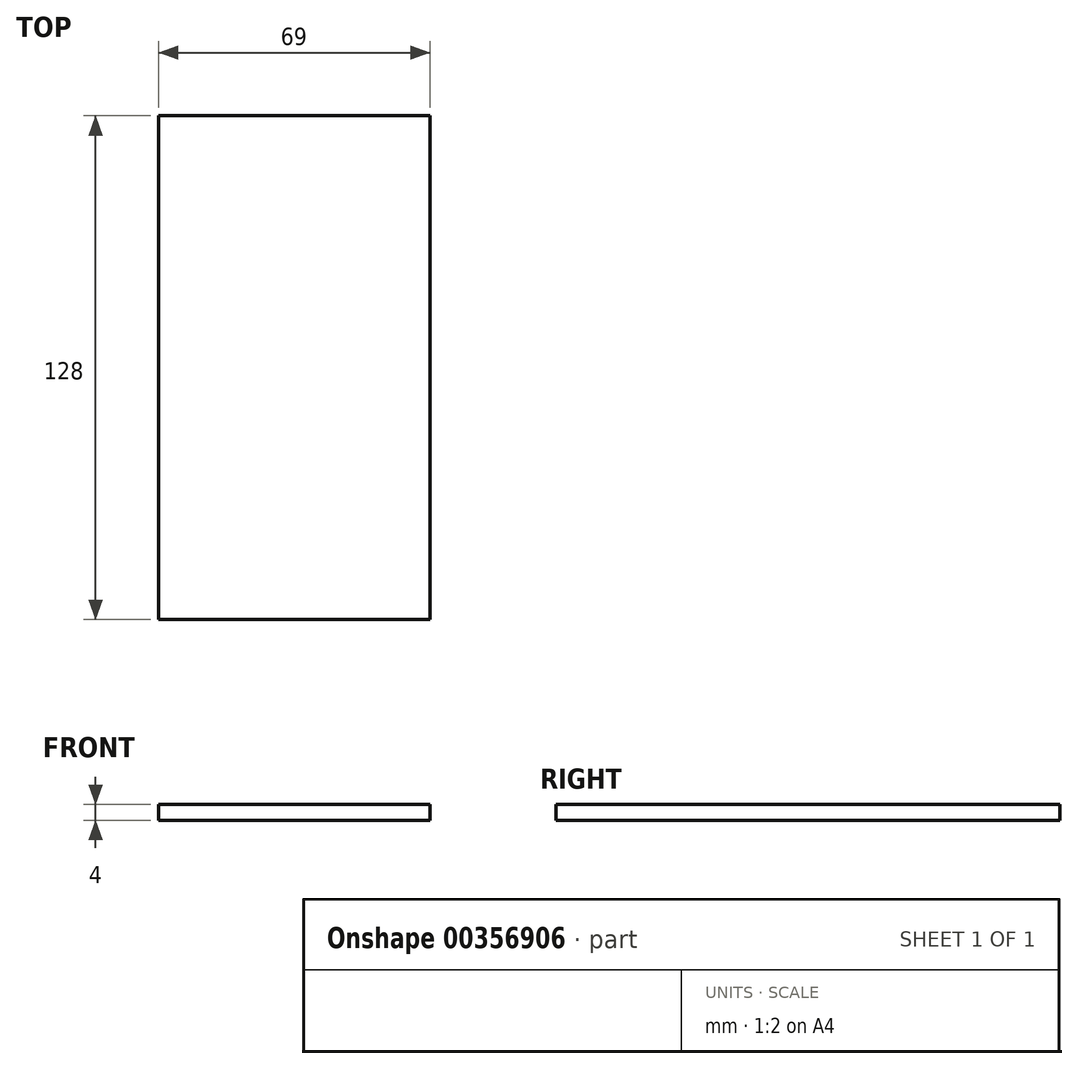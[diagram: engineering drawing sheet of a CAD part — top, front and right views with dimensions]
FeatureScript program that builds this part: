
annotation { "Feature Type Name" : "Feature", "Feature Type Description" : "" }
export const myFeature = defineFeature(function(context is Context, id is Id, definition is map)
    precondition{}
    {
        {
            var Q0;
            Q0=qCreatedBy(makeId("Top.planeOp"),FACE);
            var sketch = newSketch(context, id + "F0", { "sketchPlane" : qUnion([Q0])});
            skLineSegment(sketch, "E0.bottom", {"start": v(-34.5, 64) * mm, "end": v(34.5, 64) * mm});
            skLineSegment(sketch, "E0.top", {"start": v(-34.5, -64) * mm, "end": v(34.5, -64) * mm});
            skLineSegment(sketch, "E0.left", {"start": v(-34.5, 64) * mm, "end": v(-34.5, -64) * mm});
            skLineSegment(sketch, "E0.right", {"start": v(34.5, 64) * mm, "end": v(34.5, -64) * mm});
            skPoint(sketch, "E0.middle", {"position": v(0, 0) * mm});
            skSolve(sketch);
        }
        {
            var Q0;
            Q0=qSketchRegion(id+"F0",true);
            extrude(context, id + "F1", {"entities" : qUnion([Q0]), "depth" : 4 * mm});
        }
    });
